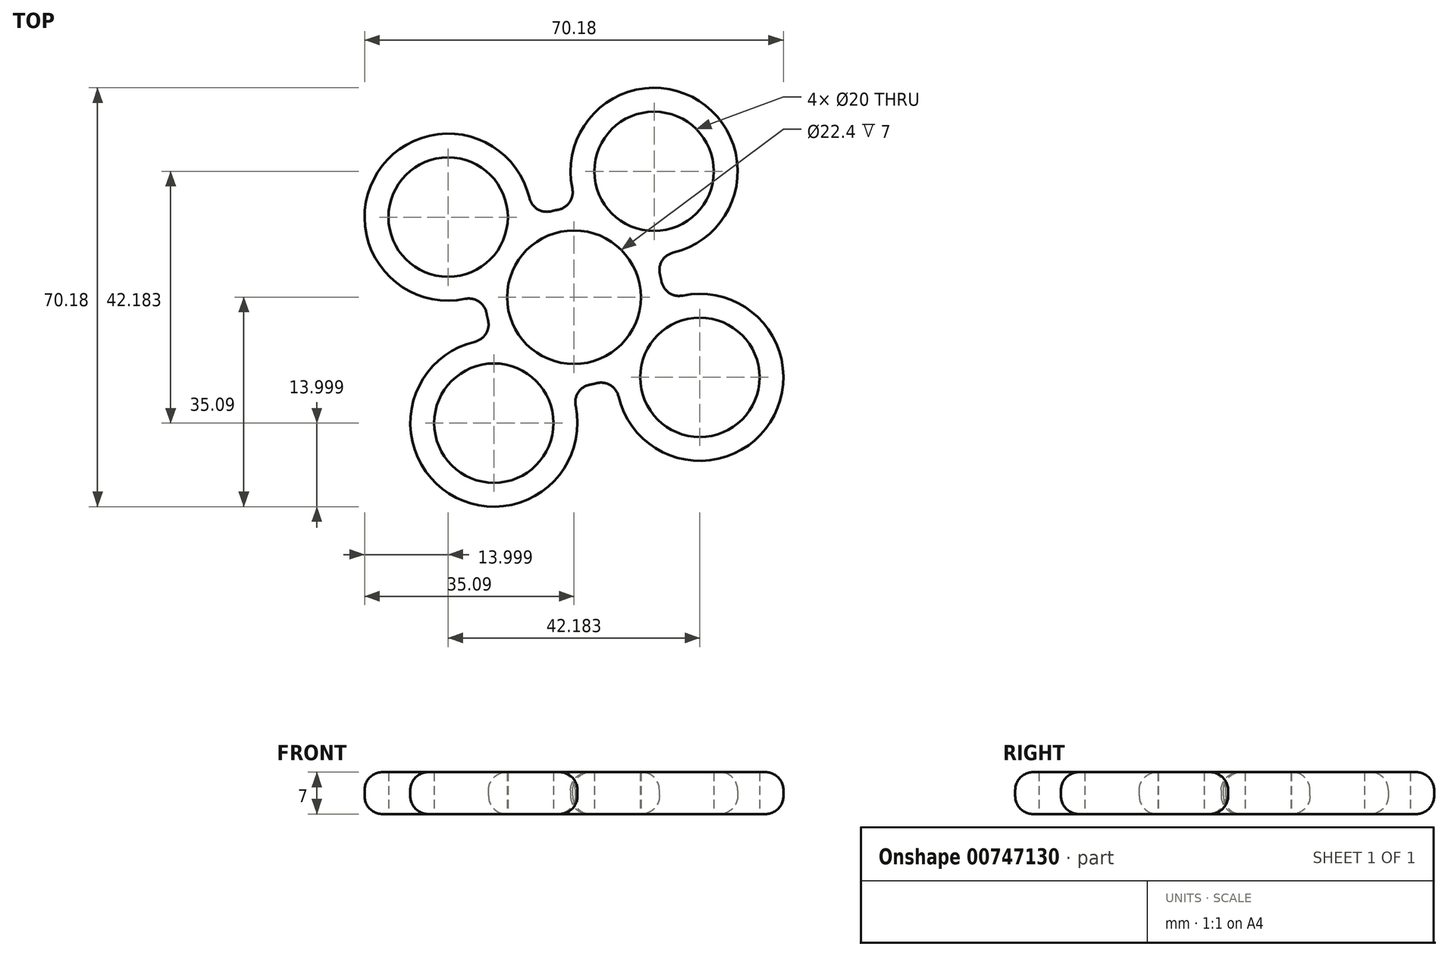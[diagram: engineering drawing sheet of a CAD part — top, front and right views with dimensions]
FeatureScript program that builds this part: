
annotation { "Feature Type Name" : "Feature", "Feature Type Description" : "" }
export const myFeature = defineFeature(function(context is Context, id is Id, definition is map)
    precondition{}
    {
        {
            var Q0;
            Q0=qCreatedBy(makeId("Top.planeOp"),FACE);
            var sketch = newSketch(context, id + "F0", { "sketchPlane" : qUnion([Q0])});
            skCircle(sketch, "E0", {"center": v(0, 0) * mm, "radius": 11.2 * mm});
            skCircle(sketch, "E1", {"center": v(0, 0) * mm, "radius": 14.9 * mm});
            skLineSegment(sketch, "E2", {"start": v(0, 0) * mm, "end": v(37.65, 59.16) * mm, "construction": true});
            skCircle(sketch, "E3", {"center": v(13.42, 21.1) * mm, "radius": 10 * mm});
            skCircle(sketch, "E4", {"center": v(13.42, 21.1) * mm, "radius": 14 * mm});
            skLineSegment(sketch, "E5.anchor1", {"start": v(0, 0) * mm, "end": v(13.42, 21.1) * mm, "construction": true});
            skLineSegment(sketch, "E6.anchor2", {"start": v(0, 0) * mm, "end": v(-18.56, 11.81) * mm, "construction": true});
            skCircle(sketch, "E7", {"center": v(0, 0) * mm, "radius": 27.63 * mm, "construction": true});
            skCircle(sketch, "E8.1.0", {"center": v(21.1, -13.42) * mm, "radius": 14 * mm});
            skCircle(sketch, "E8.1.1", {"center": v(21.1, -13.42) * mm, "radius": 10 * mm});
            skCircle(sketch, "E8.2.0", {"center": v(-13.42, -21.1) * mm, "radius": 14 * mm});
            skCircle(sketch, "E8.2.1", {"center": v(-13.42, -21.1) * mm, "radius": 10 * mm});
            skCircle(sketch, "E8.3.0", {"center": v(-21.1, 13.42) * mm, "radius": 14 * mm});
            skCircle(sketch, "E8.3.1", {"center": v(-21.1, 13.42) * mm, "radius": 10 * mm});
            skLineSegment(sketch, "E8.anchor2", {"start": v(0, 0) * mm, "end": v(-21.1, 13.42) * mm, "construction": true});
            skSolve(sketch);
        }
        {
            var Q0;
            {var subQ0=sQuery(id+"F0.wireOp",EDGE,"E4");var subQ1=sQuery(id+"F0.wireOp",EDGE,"E1");var subQ2=makeQuery(id+"F0.imprint","INTERSECT",VERTEX,{"disambiguationData":[OD(0.0)],"derivedFrom":[subQ1,subQ0]});Q0=makeQuery(id+"F0.imprint","IMPRINT",FACE,{"disambiguationData":[TD([[makeQuery(id+"F0.imprint","IMPRINT",EDGE,{"disambiguationData":[TD([[subQ2,-1.0]])],"derivedFrom":subQ1}),-1.0]])]});}
            var Q1;
            {var subQ0=sQuery(id+"F0.wireOp",EDGE,"E4");var subQ1=sQuery(id+"F0.wireOp",EDGE,"E0");var subQ2=makeQuery(id+"F0.imprint","INTERSECT",VERTEX,{"disambiguationData":[OD(1.0)],"derivedFrom":[subQ1,subQ0]});Q1=makeQuery(id+"F0.imprint","IMPRINT",FACE,{"disambiguationData":[TD([[makeQuery(id+"F0.imprint","IMPRINT",EDGE,{"disambiguationData":[TD([[subQ2,1.0]])],"derivedFrom":subQ1}),-1.0]])]});}
            var Q2;
            {var subQ4=sQuery(id+"F0.wireOp",EDGE,"E4");var subQ7=sQuery(id+"F0.wireOp",EDGE,"E0");var subQ8=makeQuery(id+"F0.imprint","INTERSECT",VERTEX,{"disambiguationData":[OD(0.0)],"derivedFrom":[subQ7,subQ4]});Q2=makeQuery(id+"F0.imprint","IMPRINT",FACE,{"disambiguationData":[TD([[makeQuery(id+"F0.imprint","IMPRINT",EDGE,{"disambiguationData":[TD([[subQ8,1.0]])],"derivedFrom":subQ7}),-1.0]])]});}
            var Q3;
            {var subQ0=sQuery(id+"F0.wireOp",EDGE,"E4");var subQ1=sQuery(id+"F0.wireOp",EDGE,"E0");var subQ2=makeQuery(id+"F0.imprint","INTERSECT",VERTEX,{"disambiguationData":[OD(0.0)],"derivedFrom":[subQ1,subQ0]});Q3=makeQuery(id+"F0.imprint","IMPRINT",FACE,{"disambiguationData":[TD([[makeQuery(id+"F0.imprint","IMPRINT",EDGE,{"disambiguationData":[TD([[subQ2,-1.0]])],"derivedFrom":subQ1}),-1.0]])]});}
            var Q4;
            {var subQ0=sQuery(id+"F0.wireOp",EDGE,"E8.3.0");var subQ5=sQuery(id+"F0.wireOp",EDGE,"E0");var subQ9=makeQuery(id+"F0.imprint","INTERSECT",VERTEX,{"disambiguationData":[OD(0.0)],"derivedFrom":[subQ5,subQ0]});Q4=makeQuery(id+"F0.imprint","IMPRINT",FACE,{"disambiguationData":[TD([[makeQuery(id+"F0.imprint","IMPRINT",EDGE,{"disambiguationData":[TD([[subQ9,-1.0]])],"derivedFrom":subQ5}),-1.0]])]});}
            var Q5;
            {var subQ0=sQuery(id+"F0.wireOp",EDGE,"E8.3.0");var subQ1=sQuery(id+"F0.wireOp",EDGE,"E1");var subQ2=makeQuery(id+"F0.imprint","INTERSECT",VERTEX,{"disambiguationData":[OD(0.0)],"derivedFrom":[subQ1,subQ0]});Q5=makeQuery(id+"F0.imprint","IMPRINT",FACE,{"disambiguationData":[TD([[makeQuery(id+"F0.imprint","IMPRINT",EDGE,{"disambiguationData":[TD([[subQ2,-1.0]])],"derivedFrom":subQ1}),-1.0]])]});}
            var Q6;
            {var subQ0=sQuery(id+"F0.wireOp",EDGE,"E8.3.0");var subQ1=sQuery(id+"F0.wireOp",EDGE,"E0");var subQ2=makeQuery(id+"F0.imprint","INTERSECT",VERTEX,{"disambiguationData":[OD(1.0)],"derivedFrom":[subQ1,subQ0]});Q6=makeQuery(id+"F0.imprint","IMPRINT",FACE,{"disambiguationData":[TD([[makeQuery(id+"F0.imprint","IMPRINT",EDGE,{"disambiguationData":[TD([[subQ2,-1.0]])],"derivedFrom":subQ1}),-1.0]])]});}
            var Q7;
            {var subQ0=sQuery(id+"F0.wireOp",EDGE,"E8.2.0");var subQ1=sQuery(id+"F0.wireOp",EDGE,"E1");var subQ2=makeQuery(id+"F0.imprint","INTERSECT",VERTEX,{"disambiguationData":[OD(0.0)],"derivedFrom":[subQ1,subQ0]});Q7=makeQuery(id+"F0.imprint","IMPRINT",FACE,{"disambiguationData":[TD([[makeQuery(id+"F0.imprint","IMPRINT",EDGE,{"disambiguationData":[TD([[subQ2,-1.0]])],"derivedFrom":subQ1}),-1.0]])]});}
            var Q8;
            {var subQ0=sQuery(id+"F0.wireOp",EDGE,"E8.2.0");var subQ6=sQuery(id+"F0.wireOp",EDGE,"E0");var subQ9=makeQuery(id+"F0.imprint","INTERSECT",VERTEX,{"disambiguationData":[OD(0.0)],"derivedFrom":[subQ6,subQ0]});Q8=makeQuery(id+"F0.imprint","IMPRINT",FACE,{"disambiguationData":[TD([[makeQuery(id+"F0.imprint","IMPRINT",EDGE,{"disambiguationData":[TD([[subQ9,-1.0]])],"derivedFrom":subQ6}),-1.0]])]});}
            var Q9;
            {var subQ0=sQuery(id+"F0.wireOp",EDGE,"E8.2.0");var subQ1=sQuery(id+"F0.wireOp",EDGE,"E0");var subQ2=makeQuery(id+"F0.imprint","INTERSECT",VERTEX,{"disambiguationData":[OD(1.0)],"derivedFrom":[subQ1,subQ0]});Q9=makeQuery(id+"F0.imprint","IMPRINT",FACE,{"disambiguationData":[TD([[makeQuery(id+"F0.imprint","IMPRINT",EDGE,{"disambiguationData":[TD([[subQ2,-1.0]])],"derivedFrom":subQ1}),-1.0]])]});}
            var Q10;
            {var subQ0=sQuery(id+"F0.wireOp",EDGE,"E8.1.0");var subQ5=sQuery(id+"F0.wireOp",EDGE,"E0");var subQ9=makeQuery(id+"F0.imprint","INTERSECT",VERTEX,{"disambiguationData":[OD(0.0)],"derivedFrom":[subQ5,subQ0]});Q10=makeQuery(id+"F0.imprint","IMPRINT",FACE,{"disambiguationData":[TD([[makeQuery(id+"F0.imprint","IMPRINT",EDGE,{"disambiguationData":[TD([[subQ9,-1.0]])],"derivedFrom":subQ5}),-1.0]])]});}
            var Q11;
            {var subQ0=sQuery(id+"F0.wireOp",EDGE,"E8.1.0");var subQ1=sQuery(id+"F0.wireOp",EDGE,"E1");var subQ2=makeQuery(id+"F0.imprint","INTERSECT",VERTEX,{"disambiguationData":[OD(0.0)],"derivedFrom":[subQ1,subQ0]});Q11=makeQuery(id+"F0.imprint","IMPRINT",FACE,{"disambiguationData":[TD([[makeQuery(id+"F0.imprint","IMPRINT",EDGE,{"disambiguationData":[TD([[subQ2,-1.0]])],"derivedFrom":subQ1}),-1.0]])]});}
            var Q12;
            {var subQ0=sQuery(id+"F0.wireOp",EDGE,"E8.1.0");var subQ1=sQuery(id+"F0.wireOp",EDGE,"E1");var subQ2=makeQuery(id+"F0.imprint","INTERSECT",VERTEX,{"disambiguationData":[OD(1.0)],"derivedFrom":[subQ1,subQ0]});Q12=makeQuery(id+"F0.imprint","IMPRINT",FACE,{"disambiguationData":[TD([[makeQuery(id+"F0.imprint","IMPRINT",EDGE,{"disambiguationData":[TD([[subQ2,-1.0]])],"derivedFrom":subQ1}),-1.0]])]});}
            var Q13;
            Q13=makeQuery(id+"F0.imprint","IMPRINT",FACE,{"disambiguationData":[TD([[makeQuery(id+"F0.imprint","IMPRINT",EDGE,{"derivedFrom":sQuery(id+"F0.wireOp",EDGE,"E3")}),-1.0]])]});
            extrude(context, id + "F1", {"entities" : qUnion([Q0, Q1, Q2, Q3, Q4, Q5, Q6, Q7, Q8, Q9, Q10, Q11, Q12, Q13]), "depth" : 7 * mm, "offsetDistance" : 25 * mm});
        }
        {
            var Q0;
            Q0=makeQuery(id+"F1.opExtrude","CAP_EDGE",EDGE,{"disambiguationData":[OSD([sQuery(id+"F0.wireOp",EDGE,"E8.2.0")])],"isStart":true});
            var Q1;
            Q1=makeQuery(id+"F1.opExtrude","CAP_EDGE",EDGE,{"disambiguationData":[OSD([sQuery(id+"F0.wireOp",EDGE,"E8.1.0")])],"isStart":true});
            var Q2;
            Q2=makeQuery(id+"F1.opExtrude","CAP_EDGE",EDGE,{"disambiguationData":[OSD([sQuery(id+"F0.wireOp",EDGE,"E4")])],"isStart":true});
            var Q3;
            Q3=makeQuery(id+"F1.opExtrude","CAP_EDGE",EDGE,{"disambiguationData":[OSD([sQuery(id+"F0.wireOp",EDGE,"E8.3.0")])],"isStart":true});
            var Q4;
            Q4=makeQuery(id+"F1.opExtrude","CAP_EDGE",EDGE,{"disambiguationData":[OSD([sQuery(id+"F0.wireOp",EDGE,"E4")])],"isStart":false});
            var Q5;
            Q5=makeQuery(id+"F1.opExtrude","CAP_EDGE",EDGE,{"disambiguationData":[OSD([sQuery(id+"F0.wireOp",EDGE,"E8.3.0")])],"isStart":false});
            var Q6;
            Q6=makeQuery(id+"F1.opExtrude","CAP_EDGE",EDGE,{"disambiguationData":[OSD([sQuery(id+"F0.wireOp",EDGE,"E8.2.0")])],"isStart":false});
            var Q7;
            Q7=makeQuery(id+"F1.opExtrude","CAP_EDGE",EDGE,{"disambiguationData":[OSD([sQuery(id+"F0.wireOp",EDGE,"E8.1.0")])],"isStart":false});
            var Q8;
            {var subQ0=sQuery(id+"F0.wireOp",EDGE,"E1");Q8=makeQuery(id+"F1.opExtrude","SWEPT_FACE",FACE,{"disambiguationData":[OSD([subQ0]),TDD([makeQuery(id+"F0.imprint","IMPRINT",EDGE,{"disambiguationData":[TD([[makeQuery(id+"F0.imprint","INTERSECT",VERTEX,{"disambiguationData":[OD(1.0)],"derivedFrom":[subQ0,sQuery(id+"F0.wireOp",EDGE,"E8.3.0")]}),-1.0]])],"derivedFrom":subQ0})])]});}
            var Q9;
            {var subQ0=sQuery(id+"F0.wireOp",EDGE,"E1");Q9=makeQuery(id+"F1.opExtrude","SWEPT_FACE",FACE,{"disambiguationData":[OSD([subQ0]),TDD([makeQuery(id+"F0.imprint","IMPRINT",EDGE,{"disambiguationData":[TD([[makeQuery(id+"F0.imprint","INTERSECT",VERTEX,{"disambiguationData":[OD(0.0)],"derivedFrom":[subQ0,sQuery(id+"F0.wireOp",EDGE,"E4")]}),1.0]])],"derivedFrom":subQ0})])]});}
            var Q10;
            {var subQ0=sQuery(id+"F0.wireOp",EDGE,"E1");Q10=makeQuery(id+"F1.opExtrude","SWEPT_FACE",FACE,{"disambiguationData":[OSD([subQ0]),TDD([makeQuery(id+"F0.imprint","IMPRINT",EDGE,{"disambiguationData":[TD([[makeQuery(id+"F0.imprint","INTERSECT",VERTEX,{"disambiguationData":[OD(1.0)],"derivedFrom":[subQ0,sQuery(id+"F0.wireOp",EDGE,"E8.2.0")]}),-1.0]])],"derivedFrom":subQ0})])]});}
            var Q11;
            {var subQ0=sQuery(id+"F0.wireOp",EDGE,"E1");Q11=makeQuery(id+"F1.opExtrude","SWEPT_FACE",FACE,{"disambiguationData":[OSD([subQ0]),TDD([makeQuery(id+"F0.imprint","IMPRINT",EDGE,{"disambiguationData":[TD([[makeQuery(id+"F0.imprint","INTERSECT",VERTEX,{"disambiguationData":[OD(1.0)],"derivedFrom":[subQ0,sQuery(id+"F0.wireOp",EDGE,"E4")]}),-1.0]])],"derivedFrom":subQ0})])]});}
            var Q12;
            {var subQ0=sQuery(id+"F0.wireOp",EDGE,"E1");Q12=makeQuery(id+"F1.opExtrude","SWEPT_FACE",FACE,{"disambiguationData":[OSD([subQ0]),TDD([makeQuery(id+"F0.imprint","IMPRINT",EDGE,{"disambiguationData":[TD([[makeQuery(id+"F0.imprint","INTERSECT",VERTEX,{"disambiguationData":[OD(0.0)],"derivedFrom":[subQ0,sQuery(id+"F0.wireOp",EDGE,"E4")]}),-1.0]])],"derivedFrom":subQ0})])]});}
            var Q13;
            {var subQ0=sQuery(id+"F0.wireOp",EDGE,"E1");Q13=makeQuery(id+"F1.opExtrude","SWEPT_FACE",FACE,{"disambiguationData":[OSD([subQ0]),TDD([makeQuery(id+"F0.imprint","IMPRINT",EDGE,{"disambiguationData":[TD([[makeQuery(id+"F0.imprint","INTERSECT",VERTEX,{"disambiguationData":[OD(1.0)],"derivedFrom":[subQ0,sQuery(id+"F0.wireOp",EDGE,"E4")]}),1.0]])],"derivedFrom":subQ0})])]});}
            fillet(context, id + "F2", {"entities" : qUnion([Q0, Q1, Q2, Q3, Q4, Q5, Q6, Q7, Q8, Q9, Q10, Q11, Q12, Q13]), "radius" : 3 * mm, "tangentPropagation" : true, "allowEdgeOverflow" : false});
        }
    });
